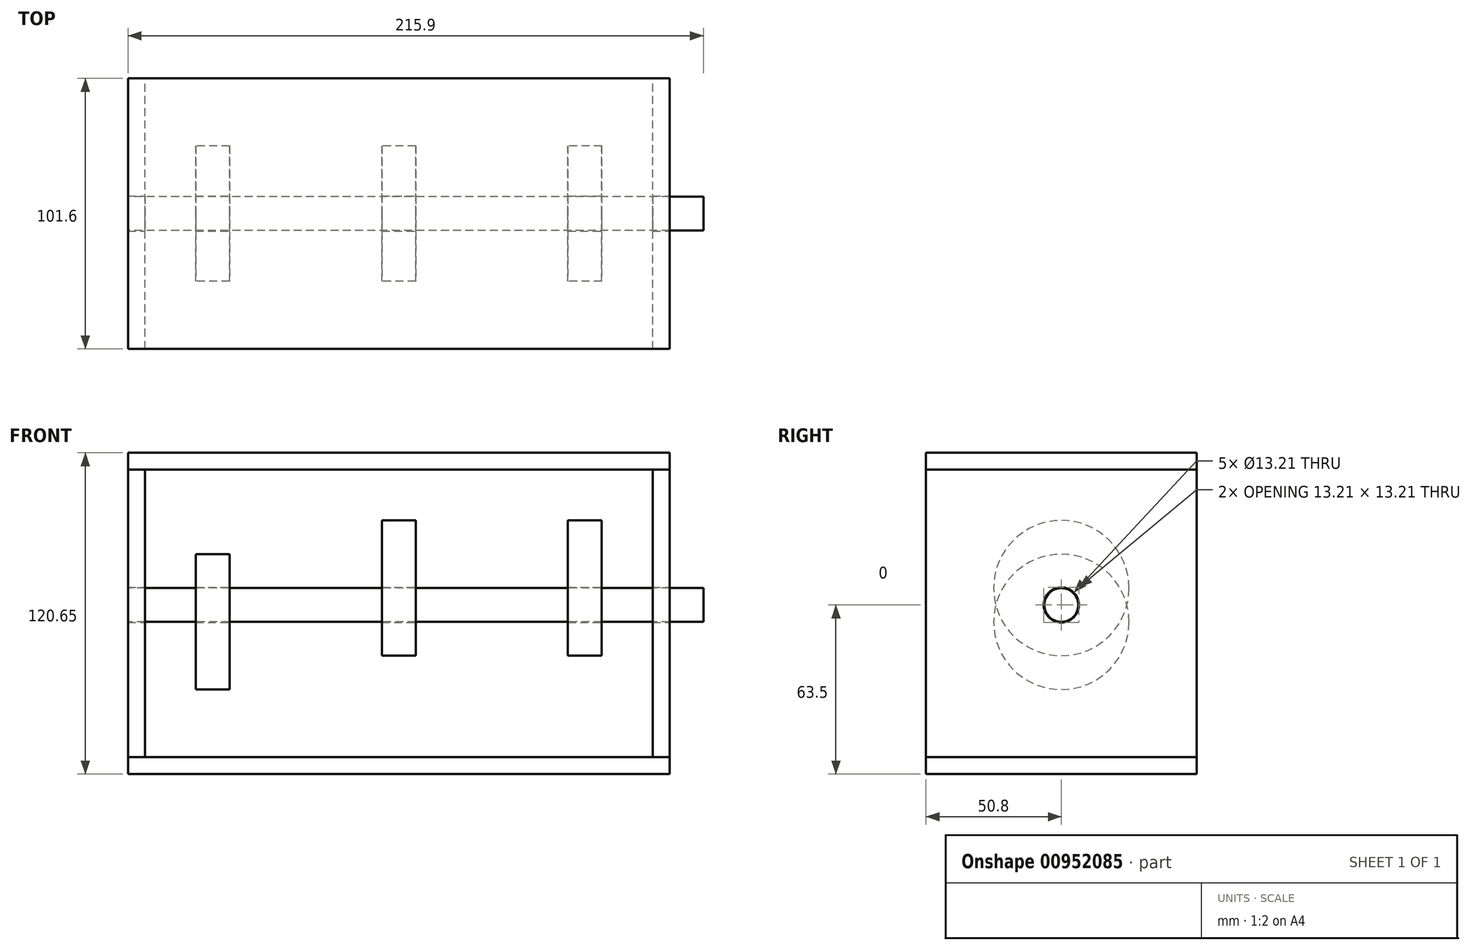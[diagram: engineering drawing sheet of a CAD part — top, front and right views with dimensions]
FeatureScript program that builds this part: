
annotation { "Feature Type Name" : "Feature", "Feature Type Description" : "" }
export const myFeature = defineFeature(function(context is Context, id is Id, definition is map)
    precondition{}
    {
        {
            var Q0;
            Q0=qCreatedBy(makeId("Front.planeOp"),FACE);
            var sketch = newSketch(context, id + "F0", { "sketchPlane" : qUnion([Q0])});
            skLineSegment(sketch, "E0", {"start": v(-101.6, 0) * mm, "end": v(101.6, 0) * mm});
            skLineSegment(sketch, "E1", {"start": v(-101.6, 0) * mm, "end": v(-101.6, 6.35) * mm});
            skLineSegment(sketch, "E2", {"start": v(-101.6, 6.35) * mm, "end": v(101.6, 6.35) * mm});
            skLineSegment(sketch, "E3", {"start": v(101.6, 6.35) * mm, "end": v(101.6, 0) * mm});
            skLineSegment(sketch, "E4", {"start": v(-101.6, 6.35) * mm, "end": v(-101.6, 120.65) * mm});
            skLineSegment(sketch, "E5", {"start": v(-101.6, 120.65) * mm, "end": v(101.6, 120.65) * mm});
            skLineSegment(sketch, "E6", {"start": v(101.6, 120.65) * mm, "end": v(101.6, 6.35) * mm});
            skLineSegment(sketch, "E7", {"start": v(-101.6, 114.3) * mm, "end": v(101.6, 114.3) * mm});
            skLineSegment(sketch, "E8", {"start": v(0, 114.3) * mm, "end": v(0, 120.65) * mm, "construction": true});
            skLineSegment(sketch, "E9", {"start": v(-95.25, 114.3) * mm, "end": v(-95.25, 6.35) * mm});
            skLineSegment(sketch, "E10", {"start": v(-95.25, 63.5) * mm, "end": v(-101.6, 63.5) * mm, "construction": true});
            skPoint(sketch, "E10.endSnap0", {"position": v(-101.6, 63.5) * mm});
            skLineSegment(sketch, "E11", {"start": v(95.25, 114.3) * mm, "end": v(95.25, 6.35) * mm});
            skLineSegment(sketch, "E12", {"start": v(95.25, 63.5) * mm, "end": v(101.6, 63.5) * mm, "construction": true});
            skLineSegment(sketch, "E13", {"start": v(0, 0) * mm, "end": v(0, 6.35) * mm, "construction": true});
            skLineSegment(sketch, "E14", {"start": v(-95.25, 63.5) * mm, "end": v(-69.85, 63.5) * mm});
            skLineSegment(sketch, "E15", {"start": v(-69.85, 63.5) * mm, "end": v(0, 63.5) * mm});
            skLineSegment(sketch, "E16", {"start": v(0, 63.5) * mm, "end": v(69.85, 63.5) * mm});
            skLineSegment(sketch, "E17", {"start": v(69.85, 63.5) * mm, "end": v(95.25, 63.5) * mm});
            skLineSegment(sketch, "E18", {"start": v(-6.35, 95.25) * mm, "end": v(6.35, 95.25) * mm});
            skLineSegment(sketch, "E19", {"start": v(6.35, 95.25) * mm, "end": v(6.35, 69.85) * mm});
            skLineSegment(sketch, "E20", {"start": v(6.35, 69.85) * mm, "end": v(6.35, 44.45) * mm});
            skLineSegment(sketch, "E21", {"start": v(6.35, 44.45) * mm, "end": v(-6.35, 44.45) * mm});
            skLineSegment(sketch, "E22", {"start": v(-6.35, 44.45) * mm, "end": v(-6.35, 69.85) * mm});
            skLineSegment(sketch, "E23", {"start": v(-6.35, 69.85) * mm, "end": v(-6.35, 95.25) * mm});
            skLineSegment(sketch, "E24", {"start": v(-6.35, 69.85) * mm, "end": v(0, 69.85) * mm});
            skLineSegment(sketch, "E25", {"start": v(0, 69.85) * mm, "end": v(6.35, 69.85) * mm});
            skLineSegment(sketch, "E26", {"start": v(0, 69.85) * mm, "end": v(0, 63.5) * mm, "construction": true});
            skLineSegment(sketch, "E27", {"start": v(76.2, 95.25) * mm, "end": v(63.5, 95.25) * mm});
            skLineSegment(sketch, "E28", {"start": v(63.5, 95.25) * mm, "end": v(63.5, 69.85) * mm});
            skLineSegment(sketch, "E29", {"start": v(63.5, 69.85) * mm, "end": v(63.5, 44.45) * mm});
            skLineSegment(sketch, "E30", {"start": v(63.5, 44.45) * mm, "end": v(76.2, 44.45) * mm});
            skLineSegment(sketch, "E31", {"start": v(76.2, 44.45) * mm, "end": v(76.2, 69.85) * mm});
            skLineSegment(sketch, "E32", {"start": v(76.2, 69.85) * mm, "end": v(76.2, 95.25) * mm});
            skLineSegment(sketch, "E33", {"start": v(63.5, 69.85) * mm, "end": v(69.85, 69.85) * mm});
            skLineSegment(sketch, "E34", {"start": v(69.85, 69.85) * mm, "end": v(76.2, 69.85) * mm});
            skLineSegment(sketch, "E35", {"start": v(69.85, 69.85) * mm, "end": v(69.85, 63.5) * mm, "construction": true});
            skLineSegment(sketch, "E36", {"start": v(-76.2, 82.55) * mm, "end": v(-76.2, 57.15) * mm});
            skLineSegment(sketch, "E37", {"start": v(-76.2, 57.15) * mm, "end": v(-76.2, 31.75) * mm});
            skLineSegment(sketch, "E38", {"start": v(-76.2, 31.75) * mm, "end": v(-63.5, 31.75) * mm});
            skLineSegment(sketch, "E39", {"start": v(-63.5, 31.75) * mm, "end": v(-63.5, 57.15) * mm});
            skLineSegment(sketch, "E40", {"start": v(-63.5, 57.15) * mm, "end": v(-63.5, 82.55) * mm});
            skLineSegment(sketch, "E41", {"start": v(-63.5, 82.55) * mm, "end": v(-76.2, 82.55) * mm});
            skLineSegment(sketch, "E42", {"start": v(-76.2, 57.15) * mm, "end": v(-69.85, 57.15) * mm});
            skLineSegment(sketch, "E43", {"start": v(-69.85, 57.15) * mm, "end": v(-63.5, 57.15) * mm});
            skLineSegment(sketch, "E44", {"start": v(-69.85, 57.15) * mm, "end": v(-69.85, 63.5) * mm, "construction": true});
            skLineSegment(sketch, "E45", {"start": v(-69.85, 63.5) * mm, "end": v(-69.85, 120.65) * mm, "construction": true});
            skLineSegment(sketch, "E46", {"start": v(69.85, 69.85) * mm, "end": v(69.85, 120.65) * mm, "construction": true});
            skSolve(sketch);
        }
        {
            var Q0;
            Q0=makeQuery(id+"F0.imprint","IMPRINT",FACE,{"disambiguationData":[TD([[makeQuery(id+"F0.imprint","IMPRINT",EDGE,{"derivedFrom":sQuery(id+"F0.wireOp",EDGE,"E0")}),1.0]])]});
            var Q1;
            {var subQ5=sQuery(id+"F0.wireOp",EDGE,"E5");Q1=makeQuery(id+"F0.imprint","IMPRINT",FACE,{"disambiguationData":[TD([[makeQuery(id+"F0.imprint","IMPRINT",EDGE,{"derivedFrom":subQ5}),-1.0]])]});}
            extrude(context, id + "F1", {"entities" : qUnion([Q0, Q1]), "endBound" : BoundingType.SYMMETRIC, "depth" : 101.6 * mm, "offsetDistance" : 25.4 * mm});
        }
        {
            var Q0;
            {var subQ1=sQuery(id+"F0.wireOp",EDGE,"E7");var subQ4=sQuery(id+"F0.wireOp",EDGE,"E4");var subQ5=makeQuery(id+"F0.imprint","INTERSECT",VERTEX,{"derivedFrom":[subQ4,subQ1]});Q0=makeQuery(id+"F0.imprint","IMPRINT",FACE,{"disambiguationData":[TD([[makeQuery(id+"F0.imprint","IMPRINT",EDGE,{"disambiguationData":[TD([[subQ5,-1.0]])],"derivedFrom":subQ1}),-1.0]])]});}
            var Q1;
            {var subQ1=sQuery(id+"F0.wireOp",EDGE,"E7");var subQ4=sQuery(id+"F0.wireOp",EDGE,"E6");var subQ5=makeQuery(id+"F0.imprint","INTERSECT",VERTEX,{"derivedFrom":[subQ4,subQ1]});Q1=makeQuery(id+"F0.imprint","IMPRINT",FACE,{"disambiguationData":[TD([[makeQuery(id+"F0.imprint","IMPRINT",EDGE,{"disambiguationData":[TD([[subQ5,1.0]])],"derivedFrom":subQ1}),-1.0]])]});}
            var Q2;
            Q2=makeQuery(id+"F1.opExtrude","CAP_FACE",FACE,{"disambiguationData":[OSD([sQuery(id+"F0.wireOp",EDGE,"E4"),sQuery(id+"F0.wireOp",EDGE,"E5"),sQuery(id+"F0.wireOp",EDGE,"E6"),sQuery(id+"F0.wireOp",EDGE,"E7")])],"isStart":false});
            var Q3;
            Q3=makeQuery(id+"F1.opExtrude","CAP_FACE",FACE,{"disambiguationData":[OSD([sQuery(id+"F0.wireOp",EDGE,"E4"),sQuery(id+"F0.wireOp",EDGE,"E5"),sQuery(id+"F0.wireOp",EDGE,"E6"),sQuery(id+"F0.wireOp",EDGE,"E7")])],"isStart":true});
            extrude(context, id + "F2", {"entities" : qUnion([Q0, Q1]), "endBound" : BoundingType.UP_TO_SURFACE, "depth" : 101.6 * mm, "endBoundEntityFace" : qUnion([Q2]), "offsetDistance" : 25.4 * mm, "hasSecondDirection" : true, "secondDirectionBound" : SecondDirectionBoundingType.UP_TO_SURFACE, "secondDirectionOppositeDirection" : true, "secondDirectionDepth" : 25.4 * mm, "secondDirectionBoundEntityFace" : qUnion([Q3])});
        }
        {
            var Q0;
            Q0=makeQuery(id+"F0.imprint","IMPRINT",FACE,{"disambiguationData":[TD([[makeQuery(id+"F0.imprint","IMPRINT",EDGE,{"derivedFrom":sQuery(id+"F0.wireOp",EDGE,"E37")}),1.0]])]});
            var Q1;
            Q1=sQuery(id+"F0.wireOp",EDGE,"E42");
            revolve(context, id + "F3", {"surfaceOperationType" : NewSurfaceOperationType.NEW, "entities" : qUnion([Q0]), "axis" : qUnion([Q1]), "revolveType" : RevolveType.FULL});
        }
        {
            var Q0;
            Q0=makeQuery(id+"F0.imprint","IMPRINT",FACE,{"disambiguationData":[TD([[makeQuery(id+"F0.imprint","IMPRINT",EDGE,{"derivedFrom":sQuery(id+"F0.wireOp",EDGE,"E18")}),-1.0]])]});
            var Q1;
            Q1=sQuery(id+"F0.wireOp",EDGE,"E25");
            revolve(context, id + "F4", {"surfaceOperationType" : NewSurfaceOperationType.NEW, "entities" : qUnion([Q0]), "axis" : qUnion([Q1]), "revolveType" : RevolveType.FULL});
        }
        {
            var Q0;
            Q0=makeQuery(id+"F0.imprint","IMPRINT",FACE,{"disambiguationData":[TD([[makeQuery(id+"F0.imprint","IMPRINT",EDGE,{"derivedFrom":sQuery(id+"F0.wireOp",EDGE,"E27")}),1.0]])]});
            var Q1;
            Q1=sQuery(id+"F0.wireOp",EDGE,"E33");
            revolve(context, id + "F5", {"surfaceOperationType" : NewSurfaceOperationType.NEW, "entities" : qUnion([Q0]), "axis" : qUnion([Q1]), "revolveType" : RevolveType.FULL});
        }
        {
            var Q0;
            Q0=makeQuery(id+"F2.opExtrude","SWEPT_FACE",FACE,{"disambiguationData":[OSD([sQuery(id+"F0.wireOp",EDGE,"E6")])]});
            var sketch = newSketch(context, id + "F6", { "sketchPlane" : qUnion([Q0])});
            skCircle(sketch, "E47", {"center": v(0, 63.5) * mm, "radius": 6.6 * mm});
            skCircle(sketch, "E48", {"center": v(0, 63.5) * mm, "radius": 6.35 * mm});
            skSolve(sketch);
        }
        {
            var Q0;
            Q0=makeQuery(id+"F6.imprint","IMPRINT",FACE,{"disambiguationData":[TD([[makeQuery(id+"F6.imprint","IMPRINT",EDGE,{"derivedFrom":sQuery(id+"F6.wireOp",EDGE,"E48")}),1.0]])]});
            var Q1;
            Q1=makeQuery(id+"F6.imprint","IMPRINT",FACE,{"disambiguationData":[TD([[makeQuery(id+"F6.imprint","IMPRINT",EDGE,{"derivedFrom":sQuery(id+"F6.wireOp",EDGE,"E47")}),1.0]])]});
            extrude(context, id + "F7", {"entities" : qUnion([Q0, Q1]), "operationType" : NewBodyOperationType.REMOVE, "endBound" : BoundingType.THROUGH_ALL, "oppositeDirection" : true, "depth" : 25.4 * mm, "offsetDistance" : 25.4 * mm});
        }
        {
            var Q0;
            Q0=makeQuery(id+"F6.imprint","IMPRINT",FACE,{"disambiguationData":[TD([[makeQuery(id+"F6.imprint","IMPRINT",EDGE,{"derivedFrom":sQuery(id+"F6.wireOp",EDGE,"E48")}),1.0]])]});
            var Q1;
            Q1=makeQuery(id+"F2.opExtrude","SWEPT_FACE",FACE,{"disambiguationData":[OSD([sQuery(id+"F0.wireOp",EDGE,"E4")])]});
            extrude(context, id + "F8", {"entities" : qUnion([Q0]), "depth" : 12.7 * mm, "offsetDistance" : 25.4 * mm, "hasSecondDirection" : true, "secondDirectionBound" : SecondDirectionBoundingType.UP_TO_SURFACE, "secondDirectionOppositeDirection" : true, "secondDirectionDepth" : 25.4 * mm, "secondDirectionBoundEntityFace" : qUnion([Q1])});
        }
        {
            var Q0;
            Q0=makeQuery(id+"F8.opExtrude","SWEPT_BODY",BODY,{"disambiguationData":[OSD([sQuery(id+"F6.wireOp",EDGE,"E48")])]});
            var Q1;
            Q1=makeQuery(id+"F3.opRevolve","SWEPT_BODY",BODY,{"disambiguationData":[OSD([sQuery(id+"F0.wireOp",EDGE,"E37"),sQuery(id+"F0.wireOp",EDGE,"E38"),sQuery(id+"F0.wireOp",EDGE,"E39"),sQuery(id+"F0.wireOp",EDGE,"E42"),sQuery(id+"F0.wireOp",EDGE,"E43")])]});
            booleanBodies(context, id + "F9", {"operationType" : BooleanOperationType.SUBTRACTION, "tools" : qUnion([Q0]), "targets" : qUnion([Q1]), "keepTools" : true});
        }
        {
            var Q0;
            Q0=makeQuery(id+"F8.opExtrude","SWEPT_BODY",BODY,{"disambiguationData":[OSD([sQuery(id+"F6.wireOp",EDGE,"E48")])]});
            var Q1;
            Q1=makeQuery(id+"F5.opRevolve","SWEPT_BODY",BODY,{"disambiguationData":[OSD([sQuery(id+"F0.wireOp",EDGE,"E27"),sQuery(id+"F0.wireOp",EDGE,"E28"),sQuery(id+"F0.wireOp",EDGE,"E32"),sQuery(id+"F0.wireOp",EDGE,"E33"),sQuery(id+"F0.wireOp",EDGE,"E34")])]});
            var Q2;
            Q2=makeQuery(id+"F4.opRevolve","SWEPT_BODY",BODY,{"disambiguationData":[OSD([sQuery(id+"F0.wireOp",EDGE,"E18"),sQuery(id+"F0.wireOp",EDGE,"E19"),sQuery(id+"F0.wireOp",EDGE,"E23"),sQuery(id+"F0.wireOp",EDGE,"E24"),sQuery(id+"F0.wireOp",EDGE,"E25")])]});
            booleanBodies(context, id + "F10", {"operationType" : BooleanOperationType.SUBTRACTION, "tools" : qUnion([Q0]), "targets" : qUnion([Q1, Q2]), "keepTools" : true});
        }
    });
